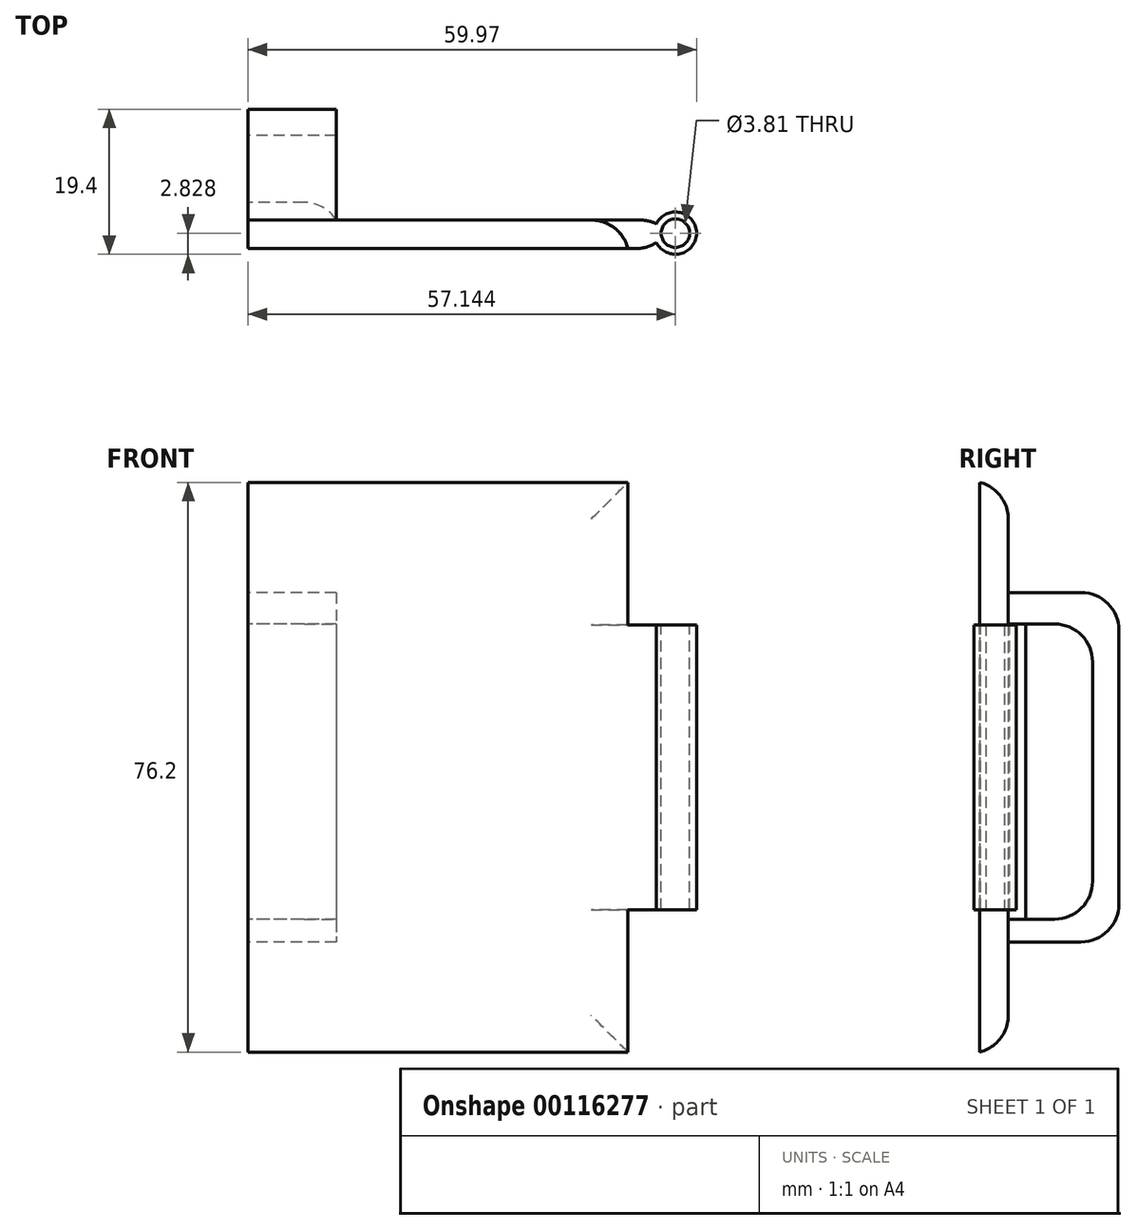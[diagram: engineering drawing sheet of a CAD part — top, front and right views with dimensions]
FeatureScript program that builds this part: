
annotation { "Feature Type Name" : "Feature", "Feature Type Description" : "" }
export const myFeature = defineFeature(function(context is Context, id is Id, definition is map)
    precondition{}
    {
        {
            var Q0;
            Q0=qCreatedBy(makeId("Front.planeOp"),FACE);
            var sketch = newSketch(context, id + "F0", { "sketchPlane" : qUnion([Q0])});
            skLineSegment(sketch, "E0.bottom", {"start": v(-50.8, 38.1) * mm, "end": v(0, 38.1) * mm});
            skLineSegment(sketch, "E0.top", {"start": v(-50.8, -38.1) * mm, "end": v(0, -38.1) * mm});
            skLineSegment(sketch, "E0.left", {"start": v(-50.8, 38.1) * mm, "end": v(-50.8, -38.1) * mm});
            skLineSegment(sketch, "E0.right", {"start": v(0, 38.1) * mm, "end": v(0, -38.1) * mm});
            skLineSegment(sketch, "E1.bottom", {"start": v(0, 19.05) * mm, "end": v(3.8, 19.05) * mm});
            skLineSegment(sketch, "E1.top", {"start": v(0, -19.05) * mm, "end": v(3.81, -19.05) * mm});
            skLineSegment(sketch, "E1.left", {"start": v(0, 19.05) * mm, "end": v(0, -19.05) * mm});
            skLineSegment(sketch, "E1.right", {"start": v(3.8, 19.05) * mm, "end": v(3.81, -19.05) * mm});
            skSolve(sketch);
        }
        {
            var Q0;
            Q0 = qSketchRegion(id + "F0", true);
            extrude(context, id + "F1", {"entities" : qUnion([Q0]), "depth" : 3.8 * mm});
        }
        {
            var Q0;
            Q0=qCreatedBy(makeId("Top.planeOp"),FACE);
            var sketch = newSketch(context, id + "F2", { "sketchPlane" : qUnion([Q0])});
            skCircle(sketch, "E2", {"center": v(6.34, -1.76) * mm, "radius": 2.83 * mm});
            skSolve(sketch);
        }
        {
            var Q0;
            Q0 = qSketchRegion(id + "F2", true);
            extrude(context, id + "F3", {"entities" : qUnion([Q0]), "operationType" : NewBodyOperationType.ADD, "depth" : 19.05 * mm, "hasSecondDirection" : true, "secondDirectionOppositeDirection" : true, "secondDirectionDepth" : 19.05 * mm});
        }
        {
            var Q0;
            Q0=makeQuery(id+"F3.boolean.opBoolean","MERGE",FACE,{"derivedFrom":[makeQuery(id+"F1.opExtrude","SWEPT_FACE",FACE,{"disambiguationData":[OSD([sQuery(id+"F0.wireOp",EDGE,"E1.bottom")])]}),makeQuery(id+"F3.opExtrude","CAP_FACE",FACE,{"disambiguationData":[OSD([sQuery(id+"F2.wireOp",EDGE,"E2")])],"isStart":false})]});
            var sketch = newSketch(context, id + "F4", { "sketchPlane" : qUnion([Q0])});
            skCircle(sketch, "E3", {"center": v(6.34, -1.76) * mm, "radius": 1.9 * mm});
            skSolve(sketch);
        }
        {
            var Q0;
            Q0 = qSketchRegion(id + "F4", true);
            extrude(context, id + "F5", {"entities" : qUnion([Q0]), "operationType" : NewBodyOperationType.REMOVE, "oppositeDirection" : true, "depth" : 47.02 * mm});
        }
        {
            var Q0;
            Q0=makeQuery(id+"F1.opExtrude","CAP_FACE",FACE,{"disambiguationData":[OSD([sQuery(id+"F0.wireOp",EDGE,"E0.bottom"),sQuery(id+"F0.wireOp",EDGE,"E0.top"),sQuery(id+"F0.wireOp",EDGE,"E0.left"),sQuery(id+"F0.wireOp",EDGE,"E0.right"),sQuery(id+"F0.wireOp",EDGE,"E1.bottom"),sQuery(id+"F0.wireOp",EDGE,"E1.top"),sQuery(id+"F0.wireOp",EDGE,"E1.right")])],"isStart":true});
            var sketch = newSketch(context, id + "F6", { "sketchPlane" : qUnion([Q0])});
            skLineSegment(sketch, "E4.bottom", {"start": v(39, 23.37) * mm, "end": v(50.8, 23.37) * mm});
            skLineSegment(sketch, "E4.top", {"start": v(39, -23.37) * mm, "end": v(50.8, -23.37) * mm});
            skLineSegment(sketch, "E4.left", {"start": v(39, 23.37) * mm, "end": v(39, -23.37) * mm});
            skLineSegment(sketch, "E4.right", {"start": v(50.8, 23.37) * mm, "end": v(50.8, -23.37) * mm});
            skLineSegment(sketch, "E5.bottom", {"start": v(50.8, -38.1) * mm, "end": v(38.3, -38.1) * mm});
            skLineSegment(sketch, "E5.top", {"start": v(50.8, 38.1) * mm, "end": v(38.3, 38.1) * mm});
            skLineSegment(sketch, "E5.left", {"start": v(50.8, -38.1) * mm, "end": v(50.8, 38.1) * mm});
            skLineSegment(sketch, "E5.right", {"start": v(38.3, -38.1) * mm, "end": v(38.3, 38.1) * mm});
            skSolve(sketch);
        }
        {
            var Q0;
            {var subQ0=sQuery(id+"F6.wireOp",EDGE,"E4.bottom");Q0=makeQuery(id+"F6.imprint","IMPRINT",FACE,{"disambiguationData":[TD([[makeQuery(id+"F6.imprint","IMPRINT",EDGE,{"derivedFrom":subQ0}),-1.0]])]});}
            var Q1;
            {var subQ0=sQuery(id+"F6.wireOp",EDGE,"E4.bottom");Q1=makeQuery(id+"F6.imprint","IMPRINT",FACE,{"disambiguationData":[TD([[makeQuery(id+"F6.imprint","IMPRINT",EDGE,{"derivedFrom":subQ0}),-1.0]])]});}
            extrude(context, id + "F7", {"entities" : qUnion([Q0, Q1]), "operationType" : NewBodyOperationType.ADD, "depth" : 14.8 * mm});
        }
        {
            var Q0;
            Q0=makeQuery(id+"F7.boolean.opBoolean","MERGE",FACE,{"derivedFrom":[makeQuery(id+"F1.opExtrude","SWEPT_FACE",FACE,{"disambiguationData":[OSD([sQuery(id+"F0.wireOp",EDGE,"E0.left")])]}),makeQuery(id+"F7.opExtrude","SWEPT_FACE",FACE,{"disambiguationData":[OSD([sQuery(id+"F6.wireOp",EDGE,"E5.left")])]})]});
            var sketch = newSketch(context, id + "F8", { "sketchPlane" : qUnion([Q0])});
            skLineSegment(sketch, "E6.bottom", {"start": v(-11.28, 19.15) * mm, "end": v(-2.35, 19.15) * mm});
            skLineSegment(sketch, "E6.top", {"start": v(-11.28, -20.33) * mm, "end": v(-2.35, -20.33) * mm});
            skLineSegment(sketch, "E6.left", {"start": v(-11.28, 19.15) * mm, "end": v(-11.28, -20.33) * mm});
            skLineSegment(sketch, "E6.right", {"start": v(-2.35, 19.15) * mm, "end": v(-2.35, -20.33) * mm});
            skSolve(sketch);
        }
        {
            var Q0;
            Q0 = qSketchRegion(id + "F8", true);
            extrude(context, id + "F9", {"entities" : qUnion([Q0]), "operationType" : NewBodyOperationType.REMOVE, "oppositeDirection" : true, "depth" : 25.4 * mm});
        }
        {
            var Q0;
            Q0=makeQuery(id+"F7.opExtrude","CAP_EDGE",EDGE,{"disambiguationData":[OSD([sQuery(id+"F6.wireOp",EDGE,"E4.top")])],"isStart":false});
            var Q1;
            Q1=makeQuery(id+"F7.opExtrude","CAP_EDGE",EDGE,{"disambiguationData":[OSD([sQuery(id+"F6.wireOp",EDGE,"E4.bottom")])],"isStart":false});
            var Q2;
            Q2=makeQuery(id+"F9.boolean.opBoolean","COPY",EDGE,{"derivedFrom":makeQuery(id+"F9.opExtrude","SWEPT_EDGE",EDGE,{"disambiguationData":[OSD([sQuery(id+"F8.wireOp",EDGE,"E6.top"),sQuery(id+"F8.wireOp",EDGE,"E6.left")])]})});
            var Q3;
            Q3=makeQuery(id+"F9.boolean.opBoolean","COPY",EDGE,{"derivedFrom":makeQuery(id+"F9.opExtrude","SWEPT_EDGE",EDGE,{"disambiguationData":[OSD([sQuery(id+"F8.wireOp",EDGE,"E6.bottom"),sQuery(id+"F8.wireOp",EDGE,"E6.left")])]})});
            var Q4;
            Q4=makeQuery(id+"F9.boolean.opBoolean","INTERSECT",EDGE,{"derivedFrom":[makeQuery(id+"F7.opExtrude","SWEPT_FACE",FACE,{"disambiguationData":[OSD([sQuery(id+"F6.wireOp",EDGE,"E4.left")])]}),makeQuery(id+"F9.opExtrude","SWEPT_FACE",FACE,{"disambiguationData":[OSD([sQuery(id+"F8.wireOp",EDGE,"E6.right")])]})]});
            var Q5;
            Q5=makeQuery(id+"F9.boolean.opBoolean","COPY",EDGE,{"derivedFrom":makeQuery(id+"F9.opExtrude","CAP_EDGE",EDGE,{"disambiguationData":[OSD([sQuery(id+"F8.wireOp",EDGE,"E6.right")])],"isStart":true})});
            var Q6;
            Q6=makeQuery(id+"F7.opExtrude","CAP_EDGE",EDGE,{"disambiguationData":[OSD([sQuery(id+"F6.wireOp",EDGE,"E4.bottom")])],"isStart":true});
            var Q7;
            Q7=makeQuery(id+"F7.opExtrude","CAP_EDGE",EDGE,{"disambiguationData":[OSD([sQuery(id+"F6.wireOp",EDGE,"E4.top")])],"isStart":true});
            fillet(context, id + "F10", {"entities" : qUnion([Q0, Q1, Q2, Q3, Q4, Q5, Q6, Q7]), "radius" : 5.08 * mm, "tangentPropagation" : true, "allowEdgeOverflow" : false});
        }
        {
            var Q0;
            Q0=makeQuery(id+"F1.opExtrude","CAP_EDGE",EDGE,{"disambiguationData":[OSD([sQuery(id+"F0.wireOp",EDGE,"E0.top")])],"isStart":true});
            var Q1;
            Q1=makeQuery(id+"F1.opExtrude","CAP_EDGE",EDGE,{"disambiguationData":[OSD([sQuery(id+"F0.wireOp",EDGE,"E0.bottom")])],"isStart":true});
            var Q2;
            {var subQ0=sQuery(id+"F0.wireOp",EDGE,"E0.right");Q2=makeQuery(id+"F1.opExtrude","CAP_EDGE",EDGE,{"disambiguationData":[OSD([subQ0]),TDD([makeQuery(id+"F0.imprint","IMPRINT",EDGE,{"disambiguationData":[TD([[makeQuery(id+"F0.imprint","INTERSECT",VERTEX,{"derivedFrom":[sQuery(id+"F0.wireOp",EDGE,"E0.bottom"),subQ0]}),-1.0]])],"derivedFrom":subQ0})])],"isStart":true});}
            var Q3;
            {var subQ0=sQuery(id+"F0.wireOp",EDGE,"E0.right");Q3=makeQuery(id+"F1.opExtrude","CAP_EDGE",EDGE,{"disambiguationData":[OSD([subQ0]),TDD([makeQuery(id+"F0.imprint","IMPRINT",EDGE,{"disambiguationData":[TD([[makeQuery(id+"F0.imprint","INTERSECT",VERTEX,{"derivedFrom":[sQuery(id+"F0.wireOp",EDGE,"E0.top"),subQ0]}),1.0]])],"derivedFrom":subQ0})])],"isStart":true});}
            var Q4;
            Q4=makeQuery(id+"F1.opExtrude","CAP_EDGE",EDGE,{"disambiguationData":[OSD([sQuery(id+"F0.wireOp",EDGE,"E1.right")])],"isStart":true});
            var Q5;
            Q5=makeQuery(id+"F1.opExtrude","CAP_EDGE",EDGE,{"disambiguationData":[OSD([sQuery(id+"F0.wireOp",EDGE,"E1.right")])],"isStart":false});
            fillet(context, id + "F11", {"entities" : qUnion([Q0, Q1, Q2, Q3, Q4, Q5]), "radius" : 5.08 * mm, "tangentPropagation" : true, "allowEdgeOverflow" : false});
        }
    });
